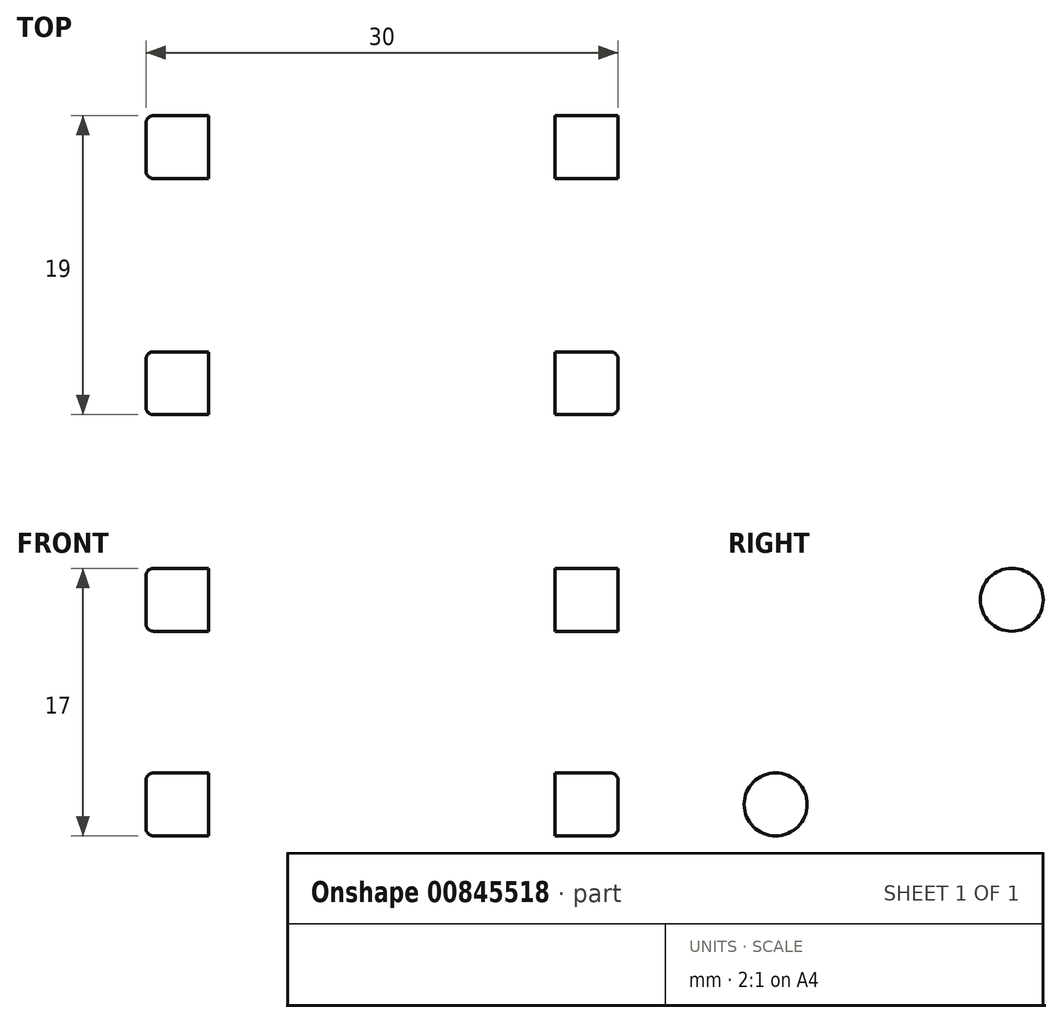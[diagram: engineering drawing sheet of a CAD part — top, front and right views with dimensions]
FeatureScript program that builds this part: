
annotation { "Feature Type Name" : "Feature", "Feature Type Description" : "" }
export const myFeature = defineFeature(function(context is Context, id is Id, definition is map)
    precondition{}
    {
        {
            var Q0;
            Q0=qCreatedBy(makeId("Top.planeOp"),FACE);
            var sketch = newSketch(context, id + "F0", { "sketchPlane" : qUnion([Q0])});
            skLineSegment(sketch, "E0.bottom", {"start": v(-15, 15) * mm, "end": v(15, 15) * mm});
            skLineSegment(sketch, "E0.top", {"start": v(-15, -15) * mm, "end": v(15, -15) * mm});
            skLineSegment(sketch, "E0.left", {"start": v(-15, 15) * mm, "end": v(-15, -15) * mm});
            skLineSegment(sketch, "E0.right", {"start": v(15, 15) * mm, "end": v(15, -15) * mm});
            skLineSegment(sketch, "E1", {"start": v(-11, 15) * mm, "end": v(-11, -11) * mm});
            skLineSegment(sketch, "E2", {"start": v(-11, -11) * mm, "end": v(11, -11) * mm});
            skLineSegment(sketch, "E3", {"start": v(11, -11) * mm, "end": v(11, 15) * mm});
            skSolve(sketch);
        }
        {
            var Q0;
            Q0=makeQuery(id+"F0.imprint","IMPRINT",FACE,{"disambiguationData":[TD([[makeQuery(id+"F0.imprint","IMPRINT",EDGE,{"derivedFrom":sQuery(id+"F0.wireOp",EDGE,"E0.top")}),1.0]])]});
            extrude(context, id + "F1", {"entities" : qUnion([Q0]), "depth" : 30 * mm, "offsetDistance" : 25 * mm});
        }
        {
            var Q0;
            {var subQ0=sQuery(id+"F0.wireOp",EDGE,"E1");Q0=makeQuery(id+"F0.imprint","IMPRINT",FACE,{"disambiguationData":[TD([[makeQuery(id+"F0.imprint","IMPRINT",EDGE,{"derivedFrom":subQ0}),1.0]])]});}
            extrude(context, id + "F2", {"entities" : qUnion([Q0]), "operationType" : NewBodyOperationType.ADD, "depth" : 4 * mm, "offsetDistance" : 25 * mm});
        }
        {
            var Q0;
            {var subQ0=sQuery(id+"F0.wireOp",EDGE,"E0.bottom");Q0=makeQuery(id+"F1.opExtrude","CAP_EDGE",EDGE,{"disambiguationData":[OSD([subQ0]),TDD([makeQuery(id+"F0.imprint","IMPRINT",EDGE,{"disambiguationData":[TD([[makeQuery(id+"F0.imprint","INTERSECT",VERTEX,{"derivedFrom":[subQ0,sQuery(id+"F0.wireOp",EDGE,"E0.left")]}),-1.0]])],"derivedFrom":subQ0})])],"isStart":false});}
            var Q1;
            {var subQ0=sQuery(id+"F0.wireOp",EDGE,"E0.bottom");Q1=makeQuery(id+"F1.opExtrude","CAP_EDGE",EDGE,{"disambiguationData":[OSD([subQ0]),TDD([makeQuery(id+"F0.imprint","IMPRINT",EDGE,{"disambiguationData":[TD([[makeQuery(id+"F0.imprint","INTERSECT",VERTEX,{"derivedFrom":[subQ0,sQuery(id+"F0.wireOp",EDGE,"E0.right")]}),1.0]])],"derivedFrom":subQ0})])],"isStart":false});}
            fillet(context, id + "F3", {"entities" : qUnion([Q0, Q1]), "radius" : 8 * mm, "tangentPropagation" : true, "allowEdgeOverflow" : false});
        }
        {
            var Q0;
            Q0=makeQuery(id+"F1.opExtrude","SWEPT_FACE",FACE,{"disambiguationData":[OSD([sQuery(id+"F0.wireOp",EDGE,"E0.right")])]});
            var sketch = newSketch(context, id + "F4", { "sketchPlane" : qUnion([Q0])});
            skCircle(sketch, "E4", {"center": v(7.5, 10.5) * mm, "radius": 2 * mm});
            skLineSegment(sketch, "E5", {"start": v(-26.72, 17) * mm, "end": v(29.52, 17) * mm, "construction": true});
            skLineSegment(sketch, "E6", {"start": v(-22.57, 4) * mm, "end": v(23.9, 4) * mm, "construction": true});
            skCircle(sketch, "E7.MirrorC", {"center": v(7.5, 23.5) * mm, "radius": 2 * mm});
            skCircle(sketch, "E8.MirrorC", {"center": v(-7.5, 23.5) * mm, "radius": 2 * mm});
            skCircle(sketch, "E9.MirrorC", {"center": v(-7.5, 10.5) * mm, "radius": 2 * mm});
            skSolve(sketch);
        }
        {
            var Q0;
            Q0=makeQuery(id+"F4.imprint","IMPRINT",FACE,{"disambiguationData":[TD([[makeQuery(id+"F4.imprint","IMPRINT",EDGE,{"derivedFrom":sQuery(id+"F4.wireOp",EDGE,"E7.MirrorC")}),-1.0]])]});
            var Q1;
            Q1=makeQuery(id+"F4.imprint","IMPRINT",FACE,{"disambiguationData":[TD([[makeQuery(id+"F4.imprint","IMPRINT",EDGE,{"derivedFrom":sQuery(id+"F4.wireOp",EDGE,"E8.MirrorC")}),1.0]])]});
            var Q2;
            Q2=makeQuery(id+"F4.imprint","IMPRINT",FACE,{"disambiguationData":[TD([[makeQuery(id+"F4.imprint","IMPRINT",EDGE,{"derivedFrom":sQuery(id+"F4.wireOp",EDGE,"E9.MirrorC")}),-1.0]])]});
            var Q3;
            Q3=makeQuery(id+"F4.imprint","IMPRINT",FACE,{"disambiguationData":[TD([[makeQuery(id+"F4.imprint","IMPRINT",EDGE,{"derivedFrom":sQuery(id+"F4.wireOp",EDGE,"E4")}),1.0]])]});
            extrude(context, id + "F5", {"entities" : qUnion([Q0, Q1, Q2, Q3]), "operationType" : NewBodyOperationType.REMOVE, "oppositeDirection" : true, "depth" : 35 * mm, "offsetDistance" : 25 * mm});
        }
        {
            var Q0;
            Q0=makeQuery(id+"F5.boolean.opBoolean","COPY",EDGE,{"derivedFrom":makeQuery(id+"F5.opExtrude","CAP_EDGE",EDGE,{"disambiguationData":[OSD([sQuery(id+"F4.wireOp",EDGE,"E9.MirrorC")])],"isStart":true})});
            var Q1;
            Q1=makeQuery(id+"F5.boolean.opBoolean","COPY",EDGE,{"derivedFrom":makeQuery(id+"F5.opExtrude","CAP_EDGE",EDGE,{"disambiguationData":[OSD([sQuery(id+"F4.wireOp",EDGE,"E4")])],"isStart":true})});
            var Q2;
            Q2=makeQuery(id+"F5.boolean.opBoolean","COPY",EDGE,{"derivedFrom":makeQuery(id+"F5.opExtrude","CAP_EDGE",EDGE,{"disambiguationData":[OSD([sQuery(id+"F4.wireOp",EDGE,"E7.MirrorC")])],"isStart":true})});
            var Q3;
            Q3=makeQuery(id+"F5.boolean.opBoolean","COPY",EDGE,{"derivedFrom":makeQuery(id+"F5.opExtrude","CAP_EDGE",EDGE,{"disambiguationData":[OSD([sQuery(id+"F4.wireOp",EDGE,"E8.MirrorC")])],"isStart":true})});
            var Q4;
            Q4=makeQuery(id+"F5.boolean.opBoolean","INTERSECT",EDGE,{"derivedFrom":[makeQuery(id+"F1.opExtrude","SWEPT_FACE",FACE,{"disambiguationData":[OSD([sQuery(id+"F0.wireOp",EDGE,"E0.left")])]}),makeQuery(id+"F5.opExtrude","SWEPT_FACE",FACE,{"disambiguationData":[OSD([sQuery(id+"F4.wireOp",EDGE,"E4")])]})]});
            var Q5;
            Q5=makeQuery(id+"F5.boolean.opBoolean","INTERSECT",EDGE,{"derivedFrom":[makeQuery(id+"F1.opExtrude","SWEPT_FACE",FACE,{"disambiguationData":[OSD([sQuery(id+"F0.wireOp",EDGE,"E0.left")])]}),makeQuery(id+"F5.opExtrude","SWEPT_FACE",FACE,{"disambiguationData":[OSD([sQuery(id+"F4.wireOp",EDGE,"E7.MirrorC")])]})]});
            var Q6;
            Q6=makeQuery(id+"F5.boolean.opBoolean","INTERSECT",EDGE,{"derivedFrom":[makeQuery(id+"F1.opExtrude","SWEPT_FACE",FACE,{"disambiguationData":[OSD([sQuery(id+"F0.wireOp",EDGE,"E0.left")])]}),makeQuery(id+"F5.opExtrude","SWEPT_FACE",FACE,{"disambiguationData":[OSD([sQuery(id+"F4.wireOp",EDGE,"E8.MirrorC")])]})]});
            var Q7;
            Q7=makeQuery(id+"F5.boolean.opBoolean","INTERSECT",EDGE,{"derivedFrom":[makeQuery(id+"F1.opExtrude","SWEPT_FACE",FACE,{"disambiguationData":[OSD([sQuery(id+"F0.wireOp",EDGE,"E0.left")])]}),makeQuery(id+"F5.opExtrude","SWEPT_FACE",FACE,{"disambiguationData":[OSD([sQuery(id+"F4.wireOp",EDGE,"E9.MirrorC")])]})]});
            fillet(context, id + "F6", {"entities" : qUnion([Q0, Q1, Q2, Q3, Q4, Q5, Q6, Q7]), "radius" : 0.5 * mm, "tangentPropagation" : true, "allowEdgeOverflow" : false});
        }
    });
